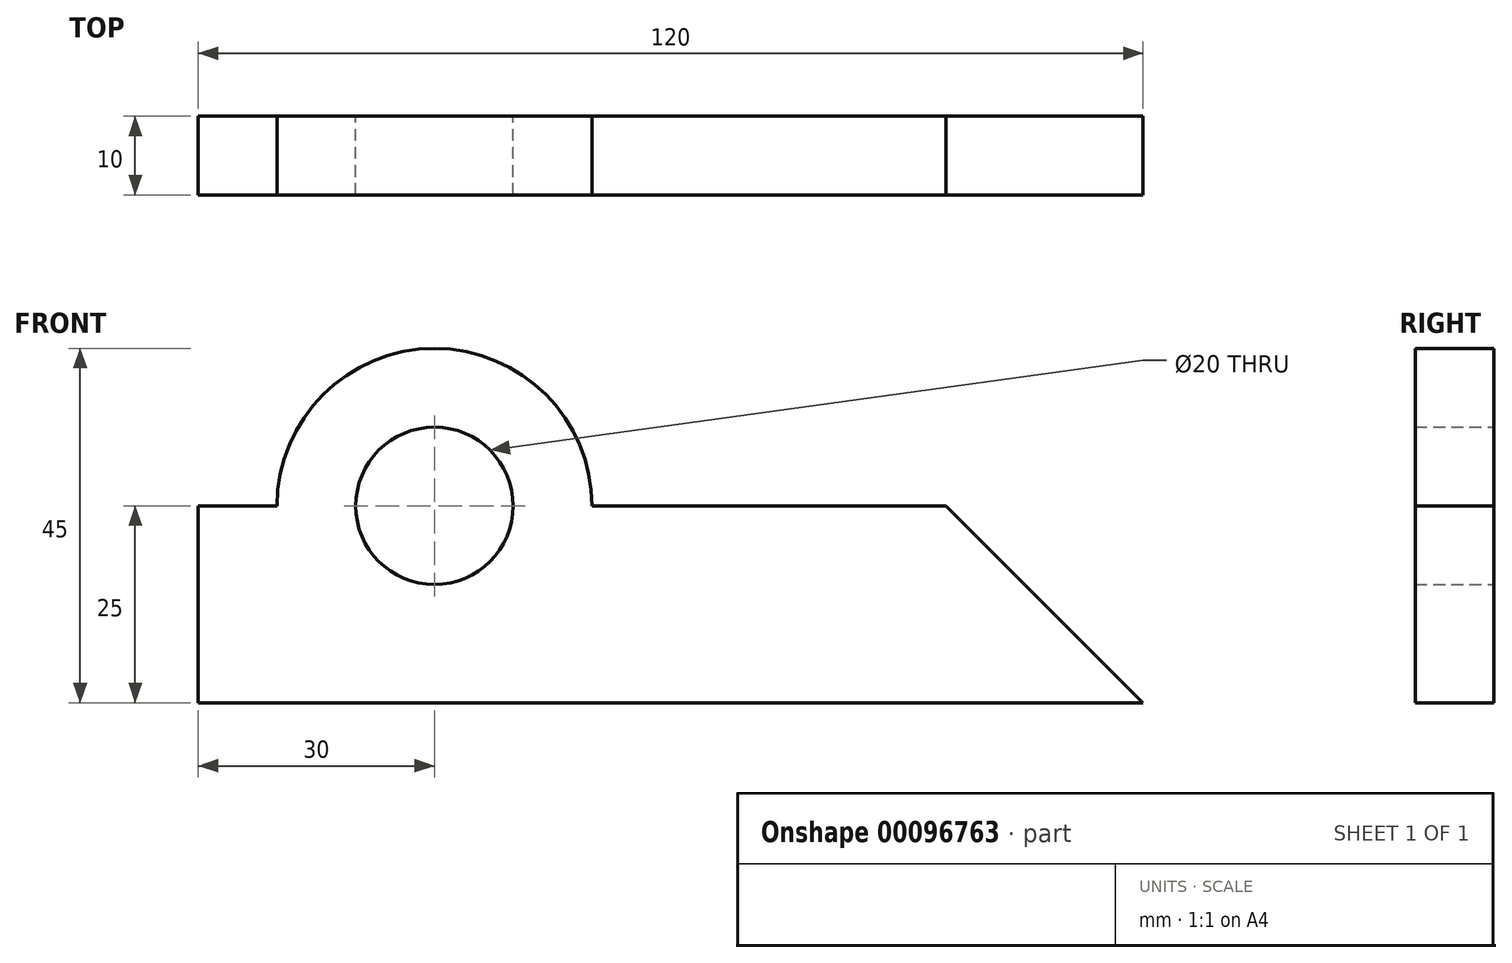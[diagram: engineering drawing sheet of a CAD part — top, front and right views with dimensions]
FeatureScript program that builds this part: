
annotation { "Feature Type Name" : "Feature", "Feature Type Description" : "" }
export const myFeature = defineFeature(function(context is Context, id is Id, definition is map)
    precondition{}
    {
        {
            var Q0;
            Q0=qCreatedBy(makeId("Front.planeOp"),FACE);
            var sketch = newSketch(context, id + "F0", { "sketchPlane" : qUnion([Q0])});
            skLineSegment(sketch, "E0", {"start": v(0, 25) * mm, "end": v(0, 0) * mm});
            skLineSegment(sketch, "E1", {"start": v(0, 0) * mm, "end": v(120, 0) * mm});
            skLineSegment(sketch, "E2", {"start": v(120, 0) * mm, "end": v(95, 25) * mm});
            skLineSegment(sketch, "E3", {"start": v(95, 25) * mm, "end": v(50, 25) * mm});
            skLineSegment(sketch, "E4", {"start": v(0, 25) * mm, "end": v(10, 25) * mm});
            skArc(sketch, "E5", {"start": v(50, 25) * mm, "mid": v(30, 45) * mm, "end": v(10, 25) * mm});
            skCircle(sketch, "E6", {"center": v(30, 25) * mm, "radius": 10 * mm});
            skSolve(sketch);
        }
        {
            var Q0;
            Q0=makeQuery(id+"F0.imprint","IMPRINT",FACE,{"disambiguationData":[TD([[makeQuery(id+"F0.imprint","IMPRINT",EDGE,{"derivedFrom":sQuery(id+"F0.wireOp",EDGE,"E0")}),1.0]])]});
            extrude(context, id + "F1", {"entities" : qUnion([Q0]), "depth" : 10 * mm});
        }
    });
